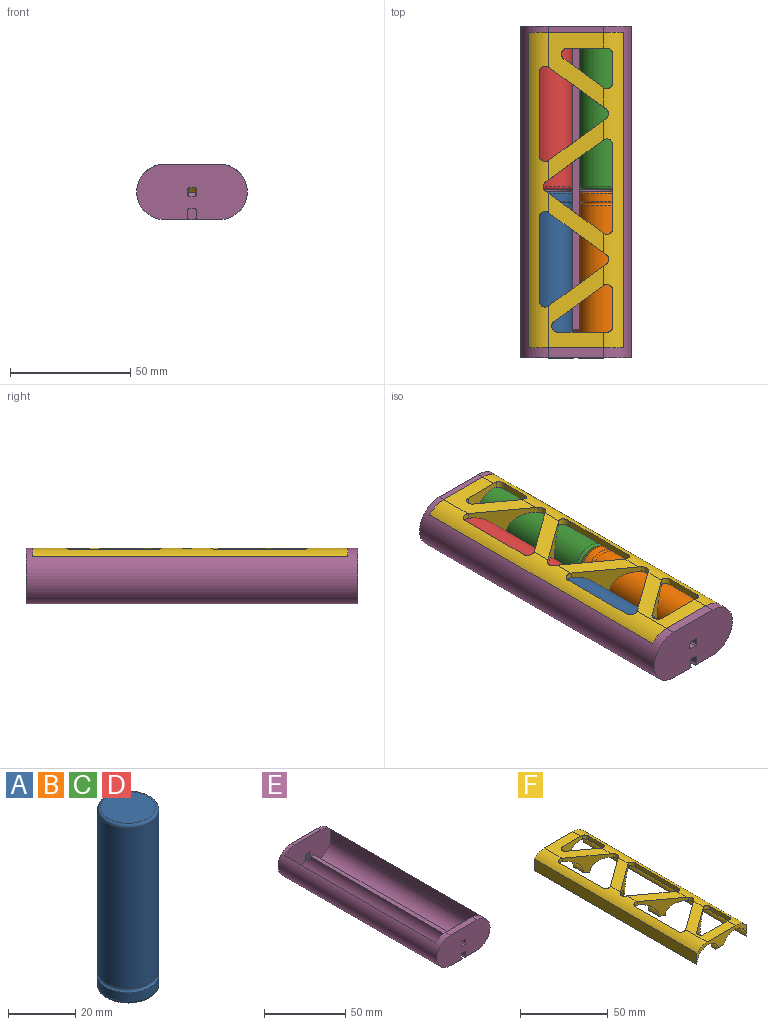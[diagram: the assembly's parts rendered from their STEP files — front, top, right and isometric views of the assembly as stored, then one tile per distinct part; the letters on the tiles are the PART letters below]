
ASSEMBLY  parts=6 mates=9
PART A: 7 faces, bbox 21x21x65 mm
  f0: cylinder r=9.15mm len=58.25mm, axis (0,0,-1), area 3348.9mm2, adj f2,f6
  f1: plane 16.3x16.3mm, normal (0,0,1), area 208.7mm2, adj f6
  f2: torus R=9.15mm, axis (0,0,1), area 128.4mm2, adj f0,f4
  f3: plane 16.3x16.3mm, normal (0,0,-1), area 208.7mm2, adj f5
  f4: cylinder r=9.15mm len=18.3mm, axis (0,0,-1), area 186.8mm2, adj f2,f5
  f5: torus R=8.15mm, axis (0,0,1), area 86.7mm2, adj f3,f4
  f6: torus R=8.15mm, axis (0,0,1), area 86.7mm2, adj f0,f1
PART B: same geometry as A
PART C: same geometry as A
PART D: same geometry as A
PART E: 54 faces, bbox 46.1x138.1x28.1 mm
  f0: plane 119.43x3mm, normal (0,0,1), area 357.9mm2, adj f5,f6,f32,f34,f35,f53
  f1: plane 46x23mm, normal (0,-1,0), area 915.7mm2, adj f7,f9,f11,f13,f15,f17,f18,f20
  f2: bspline ~5.6x5.54mm, area 9.9mm2, adj f13,f32,f40,f41
  f3: bspline ~5.6x5.54mm, area 9.9mm2, adj f18,f34,f41,f42
  f4: plane 0.5x0.13mm, normal (0,0,1), area 0mm2, adj f6,f26,f33
  f5: cylinder r=9.15mm len=131.1mm, axis (0,-1,0), area 3746.7mm2, adj f0,f26,f27,f28,f29,f31,f34,f36
  f6: cylinder r=9.15mm len=131.1mm, axis (0,-1,0), area 3746.7mm2, adj f0,f4,f26,f29,f30,f32,f33,f37
  f7: cylinder r=0.75mm len=130.59mm, axis (0,-1,0), area 151mm2, adj f1,f15,f20,f44
  f8: cylinder r=0.75mm len=0.75mm, axis (0,-1,0), area 0.2mm2, adj f16,f26,f36
  f9: cylinder r=0.75mm len=130.59mm, axis (0,-1,0), area 151mm2, adj f1,f11,f20,f38
  f10: cylinder r=0.75mm len=0.75mm, axis (0,-1,0), area 0.2mm2, adj f12,f26,f33
  f11: plane 130.59x3mm, normal (-1,0,0), area 391.8mm2, adj f1,f9,f13,f39
  f12: plane 3x0.34mm, normal (-1,0,0), area 1mm2, adj f10,f14,f26,f33
  f13: cylinder r=0.75mm len=130.59mm, axis (0,-1,0), area 150.9mm2, adj f1,f2,f11,f17,f40
  f14: cylinder r=0.75mm len=0.75mm, axis (0,-1,0), area 0.2mm2, adj f12,f26,f33
  f15: plane 130.59x3mm, normal (1,0,0), area 391.8mm2, adj f1,f7,f18,f43
  f16: plane 3x0.34mm, normal (1,0,0), area 1mm2, adj f8,f19,f26,f36
  f17: plane 126.3x2mm, normal (0,0,-1), area 252.6mm2, adj f1,f13,f18,f41
  f18: cylinder r=0.75mm len=130.59mm, axis (0,-1,0), area 150.9mm2, adj f1,f3,f15,f17,f42
  f19: cylinder r=0.75mm len=0.75mm, axis (0,-1,0), area 0.2mm2, adj f16,f26,f36
  f20: plane 138x23mm, normal (0,0,-1), area 2891.2mm2, adj f1,f7,f9,f22,f24,f25,f26,f31
  f21: plane 23x2.7mm, normal (0,0,1), area 62.1mm2, adj f22,f24,f25,f26
  f22: cylinder r=11.5mm len=138mm, axis (0,-1,0), area 3770.1mm2, adj f1,f20,f21,f23,f25,f26,f29,f30
  f23: plane 23x4.2mm, normal (0,0,1), area 96.6mm2, adj f1,f22,f24,f29
  f24: cylinder r=11.5mm len=138mm, axis (0,-1,0), area 3770.1mm2, adj f1,f20,f21,f23,f25,f26,f28,f29
  f25: plane 46x23mm, normal (0,1,0), area 944.5mm2, adj f20,f21,f22,f24
  f26: plane 39.6x23mm, normal (0,-1,0), area 729.5mm2, adj f4,f5,f6,f8,f10,f12,f14,f16
  f27: plane 0.5x0.13mm, normal (0,0,1), area 0mm2, adj f5,f26,f36
  f28: plane 131.1x7.96mm, normal (1,0,0), area 1043.5mm2, adj f5,f24,f26,f29
  f29: plane 39.6x20.65mm, normal (0,1,0), area 692.1mm2, adj f5,f6,f22,f23,f24,f28,f30,f45
  f30: plane 131.1x7.96mm, normal (-1,0,0), area 1043.5mm2, adj f6,f22,f26,f29
  f31: plane 8.52x2mm, normal (1,0,0), area 17mm2, adj f5,f20,f34,f36
  f32: cylinder r=1mm len=11.5mm, axis (0,0,-1), area 5.6mm2, adj f0,f2,f6,f20,f35,f37,f38,f39
  f33: cylinder r=1mm len=11.5mm, axis (0,0,-1), area 12.5mm2, adj f4,f6,f10,f12,f14,f20,f26,f37
  f34: cylinder r=1mm len=11.5mm, axis (0,0,-1), area 5.6mm2, adj f0,f3,f5,f20,f31,f35,f42,f43
  f35: plane 2x2mm, normal (0,1,0), area 4mm2, adj f0,f32,f34,f41
  f36: cylinder r=1mm len=11.5mm, axis (0,0,-1), area 12.5mm2, adj f5,f8,f16,f19,f20,f26,f27,f31
  f37: plane 8.52x2mm, normal (-1,0,0), area 17mm2, adj f6,f20,f32,f33
  f38: bspline ~5.75x5.71mm, area 2.8mm2, adj f9,f20,f32,f39
  f39: cylinder r=5mm len=3mm, axis (0,0,-1), area 4.3mm2, adj f11,f32,f38,f40
  f40: bspline ~2.54x2.53mm, area 1.9mm2, adj f2,f13,f32,f39
  f41: cylinder r=5mm len=5mm, axis (1,0,0), area 15.7mm2, adj f2,f3,f17,f35
  f42: bspline ~2.54x2.53mm, area 1.9mm2, adj f3,f18,f34,f43
  f43: cylinder r=5mm len=3mm, axis (0,0,-1), area 4.3mm2, adj f15,f34,f42,f44
  f44: bspline ~5.75x5.71mm, area 2.8mm2, adj f7,f20,f34,f43
  f45: cylinder r=0.75mm len=10.36mm, axis (0,-1,0), area 7.5mm2, adj f1,f5,f29,f46,f52,f53
  f46: plane 10.25x2.5mm, normal (0,0,1), area 25.6mm2, adj f1,f45,f47,f53
  f47: cylinder r=0.75mm len=10.36mm, axis (0,-1,0), area 7.5mm2, adj f1,f6,f29,f46,f48,f53
  f48: plane 4.2x2mm, normal (-1,0,0), area 8.4mm2, adj f1,f29,f47,f49
  f49: cylinder r=0.75mm len=4.2mm, axis (0,-1,0), area 4.9mm2, adj f1,f29,f48,f50
  f50: plane 4.2x2.5mm, normal (0,0,-1), area 10.5mm2, adj f1,f29,f49,f51
  f51: cylinder r=0.75mm len=4.2mm, axis (0,-1,0), area 4.9mm2, adj f1,f29,f50,f52
  f52: plane 4.2x2mm, normal (1,0,0), area 8.4mm2, adj f1,f29,f45,f51
  f53: plane 3.35x1.81mm, normal (0,-0.71,0.71), area 7.7mm2, adj f0,f5,f6,f45,f46,f47
PART F: 50 faces, bbox 39.6x131.1x11.5 mm
  f0: plane 34.01x23mm, normal (0,0,1), area 340.4mm2, adj f4,f12,f16,f32,f34,f42,f43,f44
  f1: plane 24.75x23mm, normal (0,0,1), area 184.8mm2, adj f4,f12,f26,f29,f36,f39
  f2: plane 31.04x23mm, normal (0,0,1), area 345.6mm2, adj f4,f12,f13,f18,f19,f20,f21,f37
  f3: plane 24.75x23mm, normal (0,0,1), area 184.8mm2, adj f4,f12,f25,f27,f30,f33
  f4: cylinder r=11.5mm len=131.1mm, axis (0,-1,0), area 913.4mm2, adj f0,f1,f2,f3,f13,f16,f17,f20
  f5: plane 3.5x3mm, normal (0,0,-1), area 10.5mm2, adj f10,f11,f44,f49
  f6: plane 10.21x3mm, normal (0,0,-1), area 24.1mm2, adj f10,f11,f26,f39
  f7: plane 10.21x3mm, normal (0,0,-1), area 24.1mm2, adj f10,f11,f25,f33
  f8: plane 10.21x3mm, normal (0,0,-1), area 24.1mm2, adj f10,f11,f34,f43
  f9: plane 10.21x3mm, normal (0,0,-1), area 24.1mm2, adj f10,f11,f19,f40
  f10: cylinder r=9.15mm len=131.1mm, axis (0,-1,0), area 2148.6mm2, adj f5,f6,f7,f8,f9,f13,f14,f15
  f11: cylinder r=9.15mm len=131.1mm, axis (0,-1,0), area 2137.1mm2, adj f5,f6,f7,f8,f9,f13,f14,f16
  f12: cylinder r=11.5mm len=131.1mm, axis (0,-1,0), area 906.9mm2, adj f0,f1,f2,f3,f13,f15,f16,f24
  f13: plane 39.6x11.5mm, normal (0,1,0), area 164.2mm2, adj f2,f4,f10,f11,f12,f15,f17,f48
  f14: plane 3.5x3mm, normal (0,0,-1), area 10.5mm2, adj f10,f11,f20,f48
  f15: plane 131.1x7.96mm, normal (-1,0,0), area 1043.5mm2, adj f10,f12,f13,f16
  f16: plane 39.6x11.5mm, normal (0,-1,0), area 164.2mm2, adj f0,f4,f10,f11,f12,f15,f17,f49
  f17: plane 131.1x7.96mm, normal (1,0,0), area 1043.5mm2, adj f4,f11,f13,f16
  f18: cylinder r=2.5mm len=5.76mm, axis (0,0,1), area 25.9mm2, adj f2,f10,f19,f20
  f19: plane 16.32x11.86mm, normal (0.59,0.81,0), area 121.4mm2, adj f2,f9,f10,f11,f18,f21
  f20: plane 16.32x11.5mm, normal (0,-1,0), area 94.5mm2, adj f2,f4,f10,f11,f14,f18,f23
  f21: cylinder r=2.5mm len=3.97mm, axis (0,0,1), area 14.8mm2, adj f2,f4,f11,f19,f22
  f22: plane 11.86x2.97mm, normal (-1,0,0), area 35.3mm2, adj f4,f11,f21,f23
  f23: cylinder r=2.5mm len=3.55mm, axis (0,0,1), area 11mm2, adj f4,f11,f20,f22
  f24: cylinder r=2.5mm len=4.05mm, axis (0,0,1), area 12.2mm2, adj f10,f12,f25,f26
  f25: plane 23.85x17.33mm, normal (0.59,0.81,0), area 147.8mm2, adj f3,f7,f10,f11,f12,f24,f27
  f26: plane 23.85x17.33mm, normal (0.59,-0.81,0), area 147.8mm2, adj f1,f6,f10,f11,f12,f24,f29
  f27: cylinder r=2.5mm len=3.97mm, axis (0,0,1), area 14.8mm2, adj f3,f4,f11,f25,f28
  f28: plane 34.65x2.97mm, normal (-1,0,0), area 103mm2, adj f4,f11,f27,f29
  f29: cylinder r=2.5mm len=3.97mm, axis (0,0,1), area 14.8mm2, adj f1,f4,f11,f26,f28
  f30: cylinder r=2.5mm len=3.97mm, axis (0,0,1), area 14.8mm2, adj f3,f10,f12,f31,f33
  f31: plane 34.65x2.97mm, normal (1,0,0), area 103mm2, adj f10,f12,f30,f32
  f32: cylinder r=2.5mm len=3.97mm, axis (0,0,1), area 14.8mm2, adj f0,f10,f12,f31,f34
  f33: plane 23.85x17.33mm, normal (-0.59,-0.81,0), area 147.8mm2, adj f3,f4,f7,f10,f11,f30,f35
  f34: plane 23.85x17.33mm, normal (-0.59,0.81,0), area 147.8mm2, adj f0,f4,f8,f10,f11,f32,f35
  f35: cylinder r=2.5mm len=4.05mm, axis (0,0,1), area 12.2mm2, adj f4,f11,f33,f34
  f36: cylinder r=2.5mm len=3.97mm, axis (0,0,1), area 14.8mm2, adj f1,f10,f12,f38,f39
  f37: cylinder r=2.5mm len=3.97mm, axis (0,0,1), area 14.8mm2, adj f2,f10,f12,f38,f40
  f38: plane 34.65x2.97mm, normal (1,0,0), area 103mm2, adj f10,f12,f36,f37
  f39: plane 23.85x17.33mm, normal (-0.59,0.81,0), area 147.8mm2, adj f1,f4,f6,f10,f11,f36,f41
  f40: plane 23.85x17.33mm, normal (-0.59,-0.81,0), area 147.8mm2, adj f2,f4,f9,f10,f11,f37,f41
  f41: cylinder r=2.5mm len=4.05mm, axis (0,0,1), area 12.2mm2, adj f4,f11,f39,f40
  f42: cylinder r=2.5mm len=4.52mm, axis (0,0,1), area 15.5mm2, adj f0,f10,f43,f44
  f43: plane 20.41x14.83mm, normal (0.59,-0.81,0), area 137.5mm2, adj f0,f8,f10,f11,f42,f46
  f44: plane 20.41x11.5mm, normal (0,1,0), area 111mm2, adj f0,f4,f5,f10,f11,f42,f47
  f45: plane 14.83x2.97mm, normal (-1,0,0), area 44.1mm2, adj f4,f11,f46,f47
  f46: cylinder r=2.5mm len=3.97mm, axis (0,0,1), area 14.8mm2, adj f0,f4,f11,f43,f45
  f47: cylinder r=2.5mm len=3.55mm, axis (0,0,1), area 11mm2, adj f4,f11,f44,f45
  f48: plane 4.05x3.04mm, normal (0,0.71,-0.71), area 14.1mm2, adj f10,f11,f13,f14
  f49: plane 4.05x3.04mm, normal (0,-0.71,-0.71), area 14.1mm2, adj f5,f10,f11,f16
PLACE A rot(axis=(0.48,0.62,-0.62),128.8deg) t=(0.85,69.19,11.5)mm
PLACE B rot(axis=(0.19,0.69,-0.69),158.8deg) t=(22.15,69.19,11.5)mm
PLACE C rot(axis=(0.62,0.55,-0.55),116.3deg) t=(22.15,135.07,11.5)mm
PLACE D rot(axis=(0.62,0.55,-0.55),116.3deg) t=(0.85,135.07,11.5)mm
PLACE E t=(11.5,0,11.5)mm
PLACE F t=(11.5,0,11.5)mm
MATE cylindrical C.f0 <-> E.f6  axis (0,1,0) through (22.15,100.2,11.5)mm
MATE cylindrical D.f0 <-> A.f0  axis (0,1,0) through (0.85,100.2,11.5)mm
MATE planar F.f16 <-> E.f29  axis (0,-1,0) through (11.5,4.2,19.97)mm
MATE planar F.f15 <-> E.f28  axis (-1,0,0) through (-8.3,69.75,15.48)mm
MATE planar C.f0 <-> D.f0  axis (0,-1,0) through (22.15,70.07,11.5)mm
MATE planar A.f0 <-> B.f0  axis (0,-1,0) through (0.85,4.19,11.5)mm
MATE cylindrical A.f0 <-> E.f5  axis (0,1,0) through (0.85,63.44,11.5)mm
MATE cylindrical B.f0 <-> C.f0  axis (0,1,0) through (22.15,34.31,11.5)mm
MATE planar F.f7 <-> E.f27  axis (0,0,-1) through (11.5,56.1,11.5)mm
